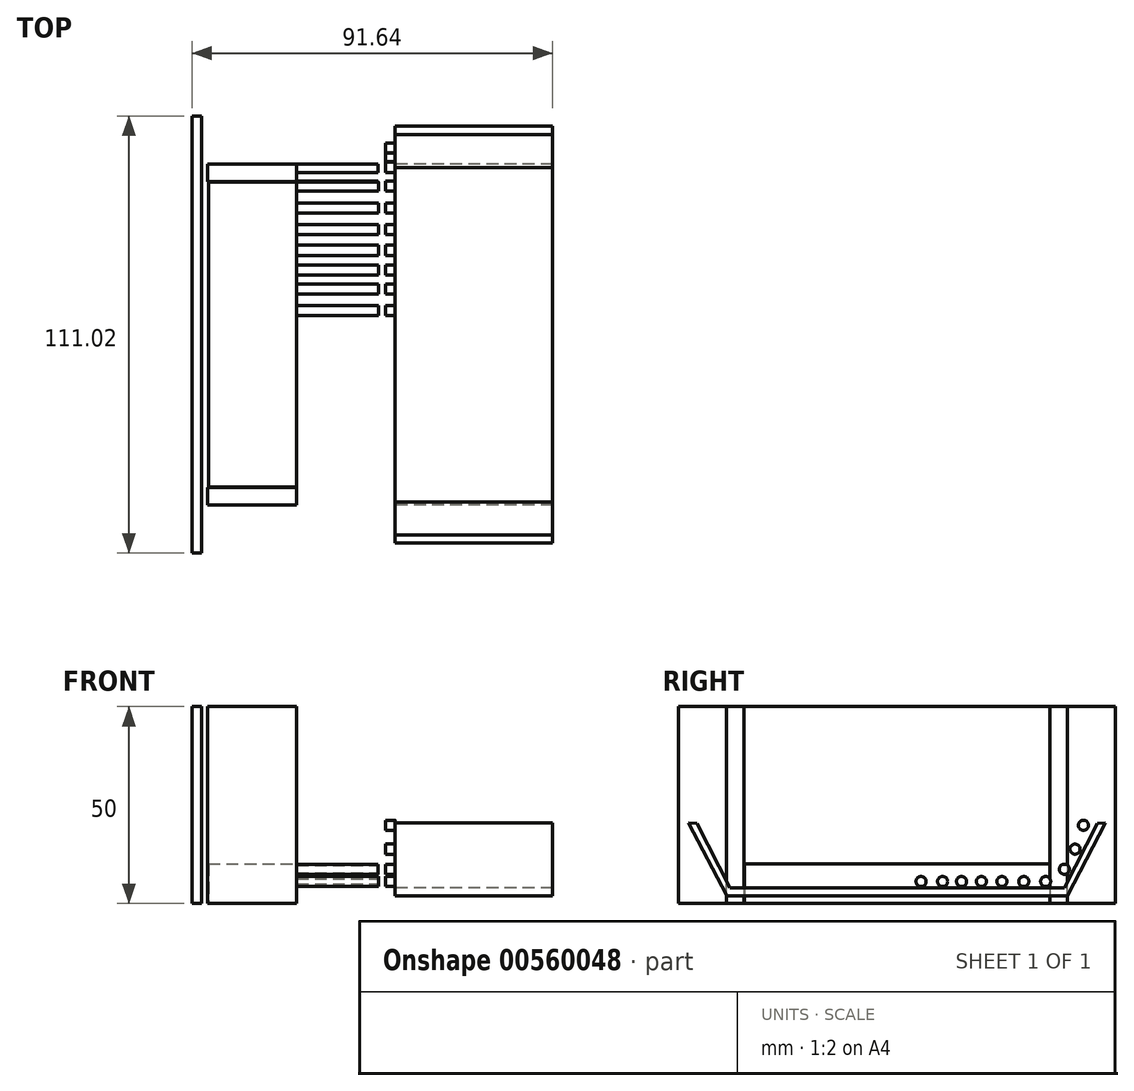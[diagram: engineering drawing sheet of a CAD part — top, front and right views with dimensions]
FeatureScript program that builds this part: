
annotation { "Feature Type Name" : "Feature", "Feature Type Description" : "" }
export const myFeature = defineFeature(function(context is Context, id is Id, definition is map)
    precondition{}
    {
        {
            var Q0;
            Q0=qCreatedBy(makeId("Top.planeOp"),FACE);
            var sketch = newSketch(context, id + "F0", { "sketchPlane" : qUnion([Q0])});
            skLineSegment(sketch, "E0.bottom", {"start": v(-21.63, 38.77) * mm, "end": v(21.63, 38.77) * mm});
            skLineSegment(sketch, "E0.top", {"start": v(-21.63, -38.77) * mm, "end": v(21.63, -38.77) * mm});
            skLineSegment(sketch, "E0.left", {"start": v(-21.63, 38.77) * mm, "end": v(-21.63, -38.77) * mm});
            skLineSegment(sketch, "E0.right", {"start": v(21.63, 38.77) * mm, "end": v(21.63, -38.77) * mm});
            skPoint(sketch, "E0.middle", {"position": v(0, 0) * mm});
            skLineSegment(sketch, "E1", {"start": v(-21.87, 38.87) * mm, "end": v(21.46, 38.87) * mm});
            skLineSegment(sketch, "E2", {"start": v(21.46, 38.87) * mm, "end": v(21.46, 43.31) * mm});
            skLineSegment(sketch, "E3", {"start": v(21.46, 43.31) * mm, "end": v(-21.87, 43.31) * mm});
            skLineSegment(sketch, "E4", {"start": v(-21.87, 43.31) * mm, "end": v(-21.87, 38.87) * mm});
            skLineSegment(sketch, "E5", {"start": v(-21.63, 0) * mm, "end": v(21.63, 0) * mm, "construction": true});
            skLineSegment(sketch, "E6.MirrorCS", {"start": v(-21.87, -38.87) * mm, "end": v(21.46, -38.87) * mm});
            skLineSegment(sketch, "E7.MirrorCS", {"start": v(21.46, -43.31) * mm, "end": v(-21.87, -43.31) * mm});
            skLineSegment(sketch, "E8.MirrorCS", {"start": v(21.46, -38.87) * mm, "end": v(21.46, -43.31) * mm});
            skLineSegment(sketch, "E9.MirrorCS", {"start": v(-21.87, -43.31) * mm, "end": v(-21.87, -38.87) * mm});
            skLineSegment(sketch, "E10", {"start": v(-23.32, 38.77) * mm, "end": v(-23.32, -47.13) * mm});
            skLineSegment(sketch, "E11", {"start": v(-25.82, -47.13) * mm, "end": v(-25.82, 38.77) * mm});
            skLineSegment(sketch, "E12", {"start": v(0, 38.77) * mm, "end": v(0, -38.77) * mm});
            skLineSegment(sketch, "E13.MirrorCS", {"start": v(23.32, 38.77) * mm, "end": v(23.32, -47.13) * mm});
            skLineSegment(sketch, "E14.MirrorCS", {"start": v(25.82, -47.13) * mm, "end": v(25.82, 38.77) * mm});
            skLineSegment(sketch, "E15", {"start": v(-25.82, -47.13) * mm, "end": v(-25.82, -55.51) * mm});
            skLineSegment(sketch, "E16", {"start": v(-25.82, -55.51) * mm, "end": v(-23.32, -55.51) * mm});
            skLineSegment(sketch, "E17", {"start": v(-23.32, -55.51) * mm, "end": v(-23.32, -47.13) * mm});
            skLineSegment(sketch, "E18", {"start": v(23.32, -47.13) * mm, "end": v(23.32, -55.51) * mm});
            skLineSegment(sketch, "E19", {"start": v(23.32, -55.51) * mm, "end": v(25.82, -55.51) * mm});
            skLineSegment(sketch, "E20", {"start": v(25.82, -55.51) * mm, "end": v(25.82, -47.13) * mm});
            skLineSegment(sketch, "E21.MirrorCS", {"start": v(-25.82, 47.13) * mm, "end": v(-25.82, 55.51) * mm});
            skLineSegment(sketch, "E22.MirrorCS", {"start": v(-23.32, 55.51) * mm, "end": v(-23.32, 47.13) * mm});
            skLineSegment(sketch, "E23.MirrorCS", {"start": v(-25.82, 55.51) * mm, "end": v(-23.32, 55.51) * mm});
            skLineSegment(sketch, "E24.MirrorCS", {"start": v(23.32, 55.51) * mm, "end": v(25.82, 55.51) * mm});
            skLineSegment(sketch, "E25.MirrorCS", {"start": v(23.32, 47.13) * mm, "end": v(23.32, 55.51) * mm});
            skLineSegment(sketch, "E26.MirrorCS", {"start": v(25.82, 55.51) * mm, "end": v(25.82, 47.13) * mm});
            skLineSegment(sketch, "E27", {"start": v(23.32, 47.13) * mm, "end": v(23.32, 38.77) * mm});
            skLineSegment(sketch, "E28", {"start": v(25.82, 47.13) * mm, "end": v(25.82, 38.77) * mm});
            skLineSegment(sketch, "E29", {"start": v(-23.32, 47.13) * mm, "end": v(-23.32, 38.77) * mm});
            skLineSegment(sketch, "E30", {"start": v(-25.82, 47.13) * mm, "end": v(-25.82, 38.77) * mm});
            skSolve(sketch);
        }
        {
            var Q0;
            {var subQ0=sQuery(id+"F0.wireOp",EDGE,"E0.right");Q0=makeQuery(id+"F0.imprint","IMPRINT",FACE,{"disambiguationData":[TD([[makeQuery(id+"F0.imprint","IMPRINT",EDGE,{"derivedFrom":subQ0}),-1.0]])]});}
            var Q1;
            {var subQ0=sQuery(id+"F0.wireOp",EDGE,"E0.left");Q1=makeQuery(id+"F0.imprint","IMPRINT",FACE,{"disambiguationData":[TD([[makeQuery(id+"F0.imprint","IMPRINT",EDGE,{"derivedFrom":subQ0}),1.0]])]});}
            extrude(context, id + "F1", {"entities" : qUnion([Q0, Q1]), "depth" : 10 * mm, "offsetDistance" : 25 * mm});
        }
        {
            var Q0;
            Q0=makeQuery(id+"F0.imprint","IMPRINT",FACE,{"disambiguationData":[TD([[makeQuery(id+"F0.imprint","IMPRINT",EDGE,{"derivedFrom":sQuery(id+"F0.wireOp",EDGE,"E1")}),1.0]])]});
            var Q1;
            Q1=makeQuery(id+"F0.imprint","IMPRINT",FACE,{"disambiguationData":[TD([[makeQuery(id+"F0.imprint","IMPRINT",EDGE,{"derivedFrom":sQuery(id+"F0.wireOp",EDGE,"E10")}),-1.0]])]});
            var Q2;
            Q2=makeQuery(id+"F0.imprint","IMPRINT",FACE,{"disambiguationData":[TD([[makeQuery(id+"F0.imprint","IMPRINT",EDGE,{"derivedFrom":sQuery(id+"F0.wireOp",EDGE,"E13.MirrorCS")}),1.0]])]});
            var Q3;
            Q3=makeQuery(id+"F0.imprint","IMPRINT",FACE,{"disambiguationData":[TD([[makeQuery(id+"F0.imprint","IMPRINT",EDGE,{"derivedFrom":sQuery(id+"F0.wireOp",EDGE,"E6.MirrorCS")}),-1.0]])]});
            extrude(context, id + "F2", {"entities" : qUnion([Q0, Q1, Q2, Q3]), "depth" : 50 * mm, "offsetDistance" : 25 * mm});
        }
        {
            var Q0;
            Q0=makeQuery(id+"F2.opExtrude","SWEPT_FACE",FACE,{"disambiguationData":[OSD([sQuery(id+"F0.wireOp",EDGE,"E14.MirrorCS")])]});
            var sketch = newSketch(context, id + "F3", { "sketchPlane" : qUnion([Q0])});
            skCircle(sketch, "E31", {"center": v(-47.35, 19.84) * mm, "radius": 1.28 * mm});
            skCircle(sketch, "E32", {"center": v(-45.23, 13.79) * mm, "radius": 1.28 * mm});
            skCircle(sketch, "E33", {"center": v(-42.5, 8.69) * mm, "radius": 1.28 * mm});
            skCircle(sketch, "E34", {"center": v(-37.76, 5.56) * mm, "radius": 1.28 * mm});
            skCircle(sketch, "E35", {"center": v(-32.2, 5.56) * mm, "radius": 1.28 * mm});
            skCircle(sketch, "E36", {"center": v(-26.64, 5.56) * mm, "radius": 1.28 * mm});
            skCircle(sketch, "E37", {"center": v(-21.43, 5.56) * mm, "radius": 1.28 * mm});
            skCircle(sketch, "E38", {"center": v(-16.39, 5.56) * mm, "radius": 1.28 * mm});
            skCircle(sketch, "E39", {"center": v(-11.57, 5.56) * mm, "radius": 1.28 * mm});
            skCircle(sketch, "E40", {"center": v(-6.1, 5.56) * mm, "radius": 1.28 * mm});
            skLineSegment(sketch, "E41", {"start": v(0, 0) * mm, "end": v(0, 50) * mm, "construction": true});
            skCircle(sketch, "E42.MirrorC", {"center": v(47.35, 19.84) * mm, "radius": 1.28 * mm});
            skCircle(sketch, "E43.MirrorC", {"center": v(45.23, 13.79) * mm, "radius": 1.28 * mm});
            skCircle(sketch, "E44.MirrorC", {"center": v(42.5, 8.69) * mm, "radius": 1.28 * mm});
            skCircle(sketch, "E45.MirrorC", {"center": v(6.1, 5.56) * mm, "radius": 1.28 * mm});
            skCircle(sketch, "E46.MirrorC", {"center": v(11.57, 5.56) * mm, "radius": 1.28 * mm});
            skCircle(sketch, "E47.MirrorC", {"center": v(16.39, 5.56) * mm, "radius": 1.28 * mm});
            skCircle(sketch, "E48.MirrorC", {"center": v(21.43, 5.56) * mm, "radius": 1.28 * mm});
            skCircle(sketch, "E49.MirrorC", {"center": v(26.64, 5.56) * mm, "radius": 1.28 * mm});
            skCircle(sketch, "E50.MirrorC", {"center": v(32.2, 5.56) * mm, "radius": 1.28 * mm});
            skCircle(sketch, "E51.MirrorC", {"center": v(37.76, 5.56) * mm, "radius": 1.28 * mm});
            skSolve(sketch);
        }
        {
            var Q0;
            Q0=makeQuery(id+"F3.imprint","IMPRINT",FACE,{"disambiguationData":[TD([[makeQuery(id+"F3.imprint","IMPRINT",EDGE,{"derivedFrom":sQuery(id+"F3.wireOp",EDGE,"E31")}),1.0]])]});
            var Q1;
            Q1=makeQuery(id+"F3.imprint","IMPRINT",FACE,{"disambiguationData":[TD([[makeQuery(id+"F3.imprint","IMPRINT",EDGE,{"derivedFrom":sQuery(id+"F3.wireOp",EDGE,"E32")}),1.0]])]});
            var Q2;
            Q2=makeQuery(id+"F3.imprint","IMPRINT",FACE,{"disambiguationData":[TD([[makeQuery(id+"F3.imprint","IMPRINT",EDGE,{"derivedFrom":sQuery(id+"F3.wireOp",EDGE,"E33")}),1.0]])]});
            var Q3;
            Q3=makeQuery(id+"F3.imprint","IMPRINT",FACE,{"disambiguationData":[TD([[makeQuery(id+"F3.imprint","IMPRINT",EDGE,{"derivedFrom":sQuery(id+"F3.wireOp",EDGE,"E34")}),1.0]])]});
            var Q4;
            Q4=makeQuery(id+"F3.imprint","IMPRINT",FACE,{"disambiguationData":[TD([[makeQuery(id+"F3.imprint","IMPRINT",EDGE,{"derivedFrom":sQuery(id+"F3.wireOp",EDGE,"E35")}),1.0]])]});
            var Q5;
            Q5=makeQuery(id+"F3.imprint","IMPRINT",FACE,{"disambiguationData":[TD([[makeQuery(id+"F3.imprint","IMPRINT",EDGE,{"derivedFrom":sQuery(id+"F3.wireOp",EDGE,"E36")}),1.0]])]});
            var Q6;
            Q6=makeQuery(id+"F3.imprint","IMPRINT",FACE,{"disambiguationData":[TD([[makeQuery(id+"F3.imprint","IMPRINT",EDGE,{"derivedFrom":sQuery(id+"F3.wireOp",EDGE,"E37")}),1.0]])]});
            var Q7;
            Q7=makeQuery(id+"F3.imprint","IMPRINT",FACE,{"disambiguationData":[TD([[makeQuery(id+"F3.imprint","IMPRINT",EDGE,{"derivedFrom":sQuery(id+"F3.wireOp",EDGE,"E38")}),1.0]])]});
            var Q8;
            Q8=makeQuery(id+"F3.imprint","IMPRINT",FACE,{"disambiguationData":[TD([[makeQuery(id+"F3.imprint","IMPRINT",EDGE,{"derivedFrom":sQuery(id+"F3.wireOp",EDGE,"E39")}),1.0]])]});
            var Q9;
            Q9=makeQuery(id+"F3.imprint","IMPRINT",FACE,{"disambiguationData":[TD([[makeQuery(id+"F3.imprint","IMPRINT",EDGE,{"derivedFrom":sQuery(id+"F3.wireOp",EDGE,"E40")}),1.0]])]});
            var Q10;
            Q10=makeQuery(id+"F3.imprint","IMPRINT",FACE,{"disambiguationData":[TD([[makeQuery(id+"F3.imprint","IMPRINT",EDGE,{"derivedFrom":sQuery(id+"F3.wireOp",EDGE,"E45.MirrorC")}),-1.0]])]});
            var Q11;
            Q11=makeQuery(id+"F3.imprint","IMPRINT",FACE,{"disambiguationData":[TD([[makeQuery(id+"F3.imprint","IMPRINT",EDGE,{"derivedFrom":sQuery(id+"F3.wireOp",EDGE,"E46.MirrorC")}),-1.0]])]});
            var Q12;
            Q12=makeQuery(id+"F3.imprint","IMPRINT",FACE,{"disambiguationData":[TD([[makeQuery(id+"F3.imprint","IMPRINT",EDGE,{"derivedFrom":sQuery(id+"F3.wireOp",EDGE,"E47.MirrorC")}),-1.0]])]});
            var Q13;
            Q13=makeQuery(id+"F3.imprint","IMPRINT",FACE,{"disambiguationData":[TD([[makeQuery(id+"F3.imprint","IMPRINT",EDGE,{"derivedFrom":sQuery(id+"F3.wireOp",EDGE,"E48.MirrorC")}),-1.0]])]});
            var Q14;
            Q14=makeQuery(id+"F3.imprint","IMPRINT",FACE,{"disambiguationData":[TD([[makeQuery(id+"F3.imprint","IMPRINT",EDGE,{"derivedFrom":sQuery(id+"F3.wireOp",EDGE,"E49.MirrorC")}),-1.0]])]});
            var Q15;
            Q15=makeQuery(id+"F3.imprint","IMPRINT",FACE,{"disambiguationData":[TD([[makeQuery(id+"F3.imprint","IMPRINT",EDGE,{"derivedFrom":sQuery(id+"F3.wireOp",EDGE,"E50.MirrorC")}),-1.0]])]});
            var Q16;
            Q16=makeQuery(id+"F3.imprint","IMPRINT",FACE,{"disambiguationData":[TD([[makeQuery(id+"F3.imprint","IMPRINT",EDGE,{"derivedFrom":sQuery(id+"F3.wireOp",EDGE,"E51.MirrorC")}),-1.0]])]});
            var Q17;
            Q17=makeQuery(id+"F3.imprint","IMPRINT",FACE,{"disambiguationData":[TD([[makeQuery(id+"F3.imprint","IMPRINT",EDGE,{"derivedFrom":sQuery(id+"F3.wireOp",EDGE,"E44.MirrorC")}),-1.0]])]});
            var Q18;
            Q18=makeQuery(id+"F3.imprint","IMPRINT",FACE,{"disambiguationData":[TD([[makeQuery(id+"F3.imprint","IMPRINT",EDGE,{"derivedFrom":sQuery(id+"F3.wireOp",EDGE,"E43.MirrorC")}),-1.0]])]});
            var Q19;
            Q19=makeQuery(id+"F3.imprint","IMPRINT",FACE,{"disambiguationData":[TD([[makeQuery(id+"F3.imprint","IMPRINT",EDGE,{"derivedFrom":sQuery(id+"F3.wireOp",EDGE,"E42.MirrorC")}),-1.0]])]});
            extrude(context, id + "F4", {"entities" : qUnion([Q0, Q1, Q2, Q3, Q4, Q5, Q6, Q7, Q8, Q9, Q10, Q11, Q12, Q13, Q14, Q15, Q16, Q17, Q18, Q19]), "operationType" : NewBodyOperationType.REMOVE, "oppositeDirection" : true, "depth" : 25 * mm, "offsetDistance" : 25 * mm});
        }
        {
            var Q0;
            Q0=makeQuery(id+"F2.opExtrude","SWEPT_FACE",FACE,{"disambiguationData":[OSD([sQuery(id+"F0.wireOp",EDGE,"E14.MirrorCS"),sQuery(id+"F0.wireOp",EDGE,"E20"),sQuery(id+"F0.wireOp",EDGE,"E26.MirrorCS"),sQuery(id+"F0.wireOp",EDGE,"E28")])]});
            var sketch = newSketch(context, id + "F5", { "sketchPlane" : qUnion([Q0])});
            skLineSegment(sketch, "E52", {"start": v(-50.86, 20.38) * mm, "end": v(-42.48, 3.9) * mm});
            skLineSegment(sketch, "E53", {"start": v(-42.48, 3.9) * mm, "end": v(0, 3.9) * mm});
            skLineSegment(sketch, "E54", {"start": v(0, 3.9) * mm, "end": v(0, 1.85) * mm});
            skLineSegment(sketch, "E55", {"start": v(0, 1.85) * mm, "end": v(-43.27, 1.85) * mm});
            skLineSegment(sketch, "E56", {"start": v(-43.27, 1.85) * mm, "end": v(-52.95, 20.5) * mm});
            skLineSegment(sketch, "E57", {"start": v(-52.95, 20.5) * mm, "end": v(-50.86, 20.38) * mm});
            skLineSegment(sketch, "E58.MirrorCS", {"start": v(43.27, 1.85) * mm, "end": v(52.95, 20.5) * mm});
            skLineSegment(sketch, "E59.MirrorCS", {"start": v(52.95, 20.5) * mm, "end": v(50.86, 20.38) * mm});
            skLineSegment(sketch, "E60.MirrorCS", {"start": v(50.86, 20.38) * mm, "end": v(42.48, 3.9) * mm});
            skLineSegment(sketch, "E61.MirrorCS", {"start": v(42.48, 3.9) * mm, "end": v(0, 3.9) * mm});
            skLineSegment(sketch, "E62.MirrorCS", {"start": v(0, 1.85) * mm, "end": v(43.27, 1.85) * mm});
            skSolve(sketch);
        }
        {
            var Q0;
            Q0=makeQuery(id+"F5.imprint","IMPRINT",FACE,{"disambiguationData":[TD([[makeQuery(id+"F5.imprint","IMPRINT",EDGE,{"derivedFrom":sQuery(id+"F5.wireOp",EDGE,"E52")}),-1.0]])]});
            var Q1;
            Q1=makeQuery(id+"F5.imprint","IMPRINT",FACE,{"disambiguationData":[TD([[makeQuery(id+"F5.imprint","IMPRINT",EDGE,{"derivedFrom":sQuery(id+"F5.wireOp",EDGE,"E54")}),1.0]])]});
            extrude(context, id + "F6", {"entities" : qUnion([Q0, Q1]), "depth" : 40 * mm, "offsetDistance" : 25 * mm});
        }
    });
